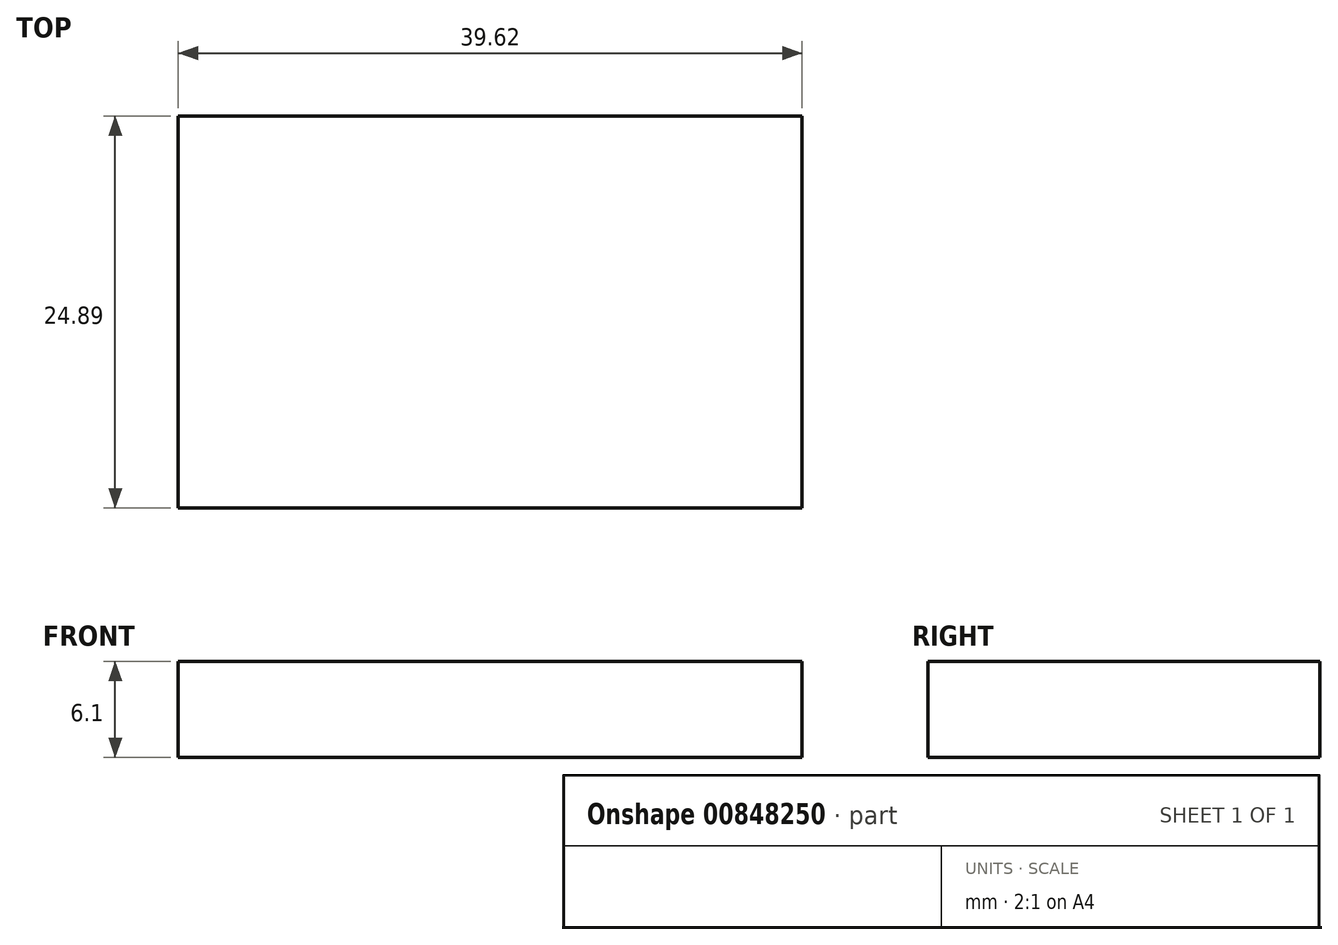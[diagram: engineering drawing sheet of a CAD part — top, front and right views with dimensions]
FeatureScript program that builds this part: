
annotation { "Feature Type Name" : "Feature", "Feature Type Description" : "" }
export const myFeature = defineFeature(function(context is Context, id is Id, definition is map)
    precondition{}
    {
        {
            var Q0;
            Q0=qCreatedBy(makeId("Top.planeOp"),FACE);
            var sketch = newSketch(context, id + "F0", { "sketchPlane" : qUnion([Q0])});
            skLineSegment(sketch, "E0.bottom", {"start": v(-51.11, 29.65) * mm, "end": v(-11.49, 29.65) * mm});
            skLineSegment(sketch, "E0.top", {"start": v(-51.11, 4.76) * mm, "end": v(-11.49, 4.76) * mm});
            skLineSegment(sketch, "E0.left", {"start": v(-51.11, 29.65) * mm, "end": v(-51.11, 4.76) * mm});
            skLineSegment(sketch, "E0.right", {"start": v(-11.49, 29.65) * mm, "end": v(-11.49, 4.76) * mm});
            skSolve(sketch);
        }
        {
            var Q0;
            Q0=makeQuery(id+"F0.imprint","IMPRINT",FACE,{"disambiguationData":[TD([[makeQuery(id+"F0.imprint","IMPRINT",EDGE,{"derivedFrom":sQuery(id+"F0.wireOp",EDGE,"E0.bottom")}),-1.0]])]});
            extrude(context, id + "F1", {"entities" : qUnion([Q0]), "depth" : 6.1 * mm, "offsetDistance" : 25.4 * mm});
        }
    });
